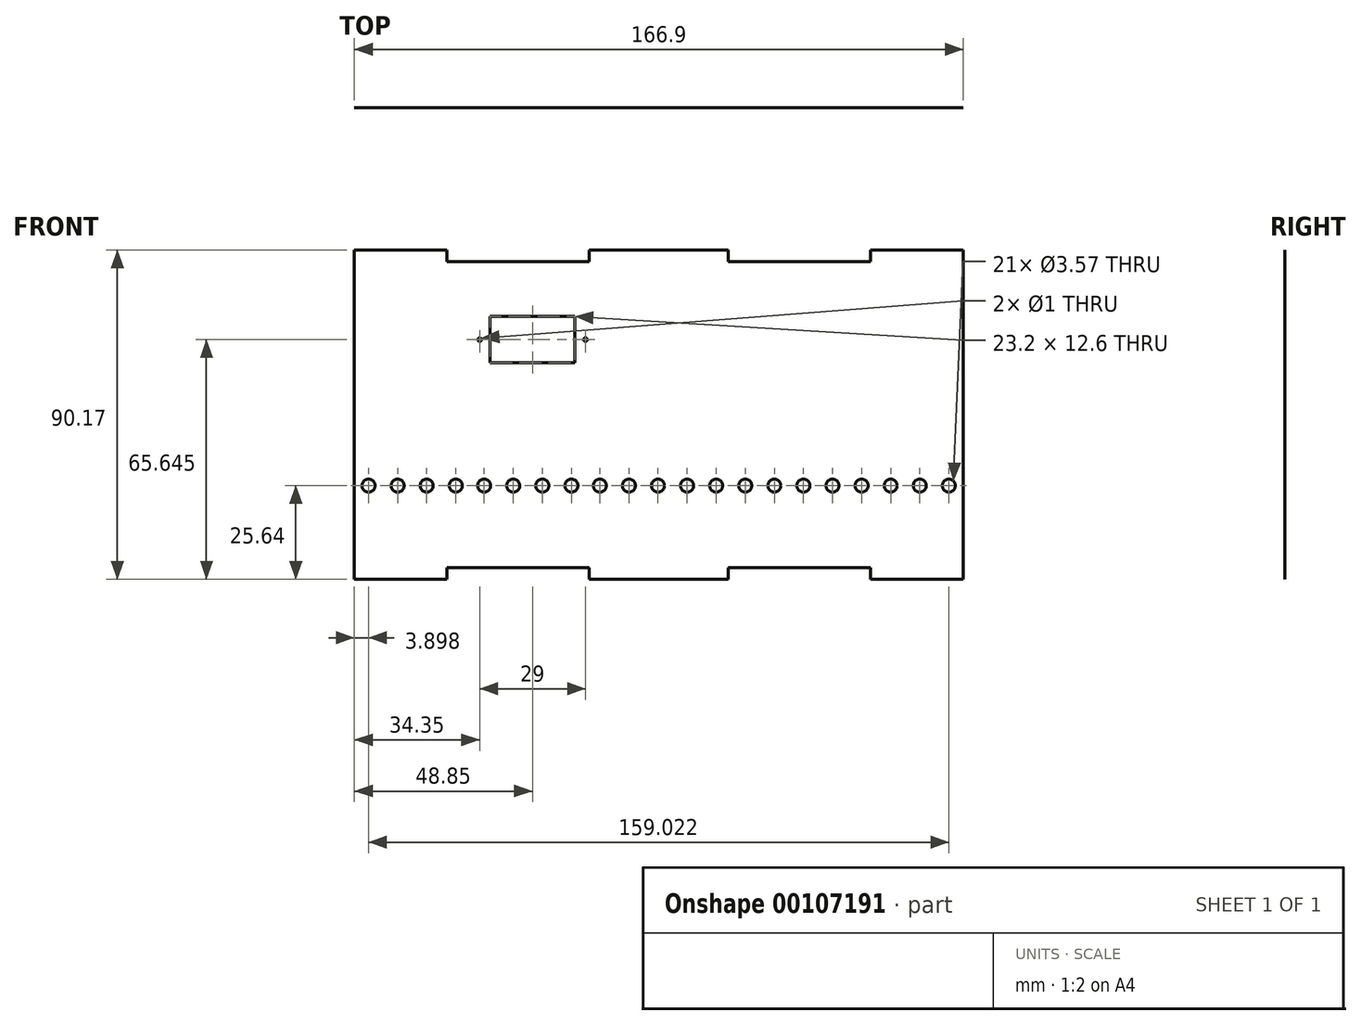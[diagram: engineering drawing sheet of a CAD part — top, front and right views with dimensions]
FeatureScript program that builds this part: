
annotation { "Feature Type Name" : "Feature", "Feature Type Description" : "" }
export const myFeature = defineFeature(function(context is Context, id is Id, definition is map)
    precondition{}
    {
        {
            var Q0;
            Q0=qCreatedBy(makeId("Front.planeOp"),FACE);
            var sketch = newSketch(context, id + "F0", { "sketchPlane" : qUnion([Q0])});
            skPoint(sketch, "E0.middle", {"position": v(0, 0) * mm});
            skCircle(sketch, "E1", {"center": v(0, 0) * mm, "radius": 1.79 * mm});
            skCircle(sketch, "E2.1.0.0", {"center": v(7.97, 0) * mm, "radius": 1.79 * mm});
            skCircle(sketch, "E2.2.0.0", {"center": v(15.94, 0) * mm, "radius": 1.79 * mm});
            skCircle(sketch, "E2.3.0.0", {"center": v(23.91, 0) * mm, "radius": 1.79 * mm});
            skCircle(sketch, "E2.4.0.0", {"center": v(31.88, 0) * mm, "radius": 1.79 * mm});
            skCircle(sketch, "E2.5.0.0", {"center": v(39.85, 0) * mm, "radius": 1.79 * mm});
            skCircle(sketch, "E2.6.0.0", {"center": v(47.82, 0) * mm, "radius": 1.79 * mm});
            skCircle(sketch, "E2.7.0.0", {"center": v(55.8, 0) * mm, "radius": 1.79 * mm});
            skCircle(sketch, "E2.8.0.0", {"center": v(63.76, 0) * mm, "radius": 1.79 * mm});
            skCircle(sketch, "E2.9.0.0", {"center": v(71.73, 0) * mm, "radius": 1.79 * mm});
            skLineSegment(sketch, "E2.direction1", {"start": v(0, 0) * mm, "end": v(7.97, 0) * mm, "construction": true});
            skCircle(sketch, "E3.MirrorC", {"center": v(-7.8, 0) * mm, "radius": 1.79 * mm});
            skCircle(sketch, "E4.MirrorC", {"center": v(-15.76, 0) * mm, "radius": 1.79 * mm});
            skCircle(sketch, "E5.MirrorC", {"center": v(-23.73, 0) * mm, "radius": 1.79 * mm});
            skCircle(sketch, "E6.MirrorC", {"center": v(-31.7, 0) * mm, "radius": 1.79 * mm});
            skCircle(sketch, "E7.MirrorC", {"center": v(-63.38, 0) * mm, "radius": 1.79 * mm});
            skCircle(sketch, "E8.MirrorC", {"center": v(-47.44, 0) * mm, "radius": 1.79 * mm});
            skCircle(sketch, "E9.MirrorC", {"center": v(-55.41, 0) * mm, "radius": 1.79 * mm});
            skCircle(sketch, "E10.MirrorC", {"center": v(-39.47, 0) * mm, "radius": 1.79 * mm});
            skLineSegment(sketch, "E11", {"start": v(-67.28, -22.47) * mm, "end": v(-67.28, 61.13) * mm});
            skPoint(sketch, "E11.startSnap0", {"position": v(-67.28, 9.2) * mm});
            skPoint(sketch, "E11.endSnap0", {"position": v(-67.28, 33.4) * mm});
            skLineSegment(sketch, "E12", {"start": v(-67.28, 61.35) * mm, "end": v(-67.28, 61.13) * mm});
            skLineSegment(sketch, "E13.top", {"start": v(99.62, 64.53) * mm, "end": v(74.22, 64.53) * mm});
            skLineSegment(sketch, "E13.left", {"start": v(99.62, 61.35) * mm, "end": v(99.62, 64.53) * mm});
            skLineSegment(sketch, "E13.right", {"start": v(74.22, 61.35) * mm, "end": v(74.22, 64.53) * mm});
            skLineSegment(sketch, "E14.top", {"start": v(35.22, 64.53) * mm, "end": v(-2.88, 64.53) * mm});
            skLineSegment(sketch, "E14.left", {"start": v(35.22, 61.35) * mm, "end": v(35.22, 64.53) * mm});
            skLineSegment(sketch, "E14.right", {"start": v(-2.88, 61.35) * mm, "end": v(-2.88, 64.53) * mm});
            skLineSegment(sketch, "E15.top", {"start": v(-67.28, 64.53) * mm, "end": v(-41.88, 64.53) * mm});
            skLineSegment(sketch, "E15.left", {"start": v(-67.28, 61.35) * mm, "end": v(-67.28, 64.53) * mm});
            skLineSegment(sketch, "E15.right", {"start": v(-41.88, 61.35) * mm, "end": v(-41.88, 64.53) * mm});
            skPoint(sketch, "E16", {"position": v(16.17, 61.35) * mm});
            skLineSegment(sketch, "E17.top", {"start": v(-67.28, -25.64) * mm, "end": v(-41.88, -25.64) * mm});
            skLineSegment(sketch, "E17.left", {"start": v(-67.28, -22.47) * mm, "end": v(-67.28, -25.64) * mm});
            skLineSegment(sketch, "E17.right", {"start": v(-41.88, -22.47) * mm, "end": v(-41.88, -25.64) * mm});
            skLineSegment(sketch, "E18.top", {"start": v(-2.88, -25.64) * mm, "end": v(35.22, -25.64) * mm});
            skLineSegment(sketch, "E18.left", {"start": v(-2.88, -22.47) * mm, "end": v(-2.88, -25.64) * mm});
            skLineSegment(sketch, "E18.right", {"start": v(35.22, -22.47) * mm, "end": v(35.22, -25.64) * mm});
            skLineSegment(sketch, "E19.top", {"start": v(99.62, -25.64) * mm, "end": v(74.22, -25.64) * mm});
            skLineSegment(sketch, "E19.left", {"start": v(99.62, -22.47) * mm, "end": v(99.62, -25.64) * mm});
            skLineSegment(sketch, "E19.right", {"start": v(74.22, -22.47) * mm, "end": v(74.22, -25.64) * mm});
            skPoint(sketch, "E20", {"position": v(16.17, -22.47) * mm});
            skCircle(sketch, "E21.7.0.0", {"center": v(79.7, 0) * mm, "radius": 1.79 * mm});
            skCircle(sketch, "E22.7.0.0", {"center": v(87.67, 0) * mm, "radius": 1.79 * mm});
            skCircle(sketch, "E23.7.0.0", {"center": v(95.64, 0) * mm, "radius": 1.79 * mm});
            skLineSegment(sketch, "E24", {"start": v(99.62, -22.47) * mm, "end": v(99.62, 61.35) * mm});
            skPoint(sketch, "E24.startSnap0", {"position": v(99.62, 3.81) * mm});
            skLineSegment(sketch, "E25", {"start": v(-41.88, 61.35) * mm, "end": v(-2.88, 61.35) * mm});
            skLineSegment(sketch, "E26", {"start": v(74.22, -22.47) * mm, "end": v(35.22, -22.47) * mm});
            skLineSegment(sketch, "E27.bottom", {"start": v(-30.03, 46.3) * mm, "end": v(-6.83, 46.3) * mm});
            skLineSegment(sketch, "E27.top", {"start": v(-30.03, 33.7) * mm, "end": v(-6.83, 33.7) * mm});
            skLineSegment(sketch, "E27.left", {"start": v(-30.03, 46.3) * mm, "end": v(-30.03, 33.7) * mm});
            skLineSegment(sketch, "E27.right", {"start": v(-6.83, 46.3) * mm, "end": v(-6.83, 33.7) * mm});
            skPoint(sketch, "E28", {"position": v(-23.73, 46.3) * mm});
            skPoint(sketch, "E29.startSnap0", {"position": v(-18.43, 40) * mm});
            skCircle(sketch, "E30", {"center": v(-3.93, 40) * mm, "radius": 0.5 * mm});
            skCircle(sketch, "E31", {"center": v(-32.93, 40) * mm, "radius": 0.5 * mm});
            skLineSegment(sketch, "E32.trimOffspring", {"start": v(35.22, 61.35) * mm, "end": v(74.22, 61.35) * mm});
            skLineSegment(sketch, "E33", {"start": v(-41.88, -22.47) * mm, "end": v(-2.88, -22.47) * mm});
            skSolve(sketch);
        }
        {
            var Q0;
            Q0=makeQuery(id+"F0.imprint","IMPRINT",FACE,{"disambiguationData":[TD([[makeQuery(id+"F0.imprint","IMPRINT",EDGE,{"derivedFrom":sQuery(id+"F0.wireOp",EDGE,"E15.top")}),-1.0]])]});
            var Q1;
            Q1=makeQuery(id+"F0.imprint","IMPRINT",FACE,{"disambiguationData":[TD([[makeQuery(id+"F0.imprint","IMPRINT",EDGE,{"derivedFrom":sQuery(id+"F0.wireOp",EDGE,"E14.top")}),1.0]])]});
            var Q2;
            Q2=makeQuery(id+"F0.imprint","IMPRINT",FACE,{"disambiguationData":[TD([[makeQuery(id+"F0.imprint","IMPRINT",EDGE,{"derivedFrom":sQuery(id+"F0.wireOp",EDGE,"E13.top")}),1.0]])]});
            var Q3;
            Q3=makeQuery(id+"F0.imprint","IMPRINT",FACE,{"disambiguationData":[TD([[makeQuery(id+"F0.imprint","IMPRINT",EDGE,{"derivedFrom":sQuery(id+"F0.wireOp",EDGE,"E19.top")}),-1.0]])]});
            var Q4;
            Q4=makeQuery(id+"F0.imprint","IMPRINT",FACE,{"disambiguationData":[TD([[makeQuery(id+"F0.imprint","IMPRINT",EDGE,{"derivedFrom":sQuery(id+"F0.wireOp",EDGE,"E18.top")}),1.0]])]});
            var Q5;
            Q5=makeQuery(id+"F0.imprint","IMPRINT",FACE,{"disambiguationData":[TD([[makeQuery(id+"F0.imprint","IMPRINT",EDGE,{"derivedFrom":sQuery(id+"F0.wireOp",EDGE,"E17.top")}),1.0]])]});
            var Q6;
            Q6=makeQuery(id+"F0.imprint","IMPRINT",FACE,{"disambiguationData":[TD([[makeQuery(id+"F0.imprint","IMPRINT",EDGE,{"derivedFrom":sQuery(id+"F0.wireOp",EDGE,"E1")}),-1.0]])]});
            extrude(context, id + "F1", {"entities" : qUnion([Q0, Q1, Q2, Q3, Q4, Q5, Q6]), "depth" : 1 / 203.2 * mm});
        }
    });
